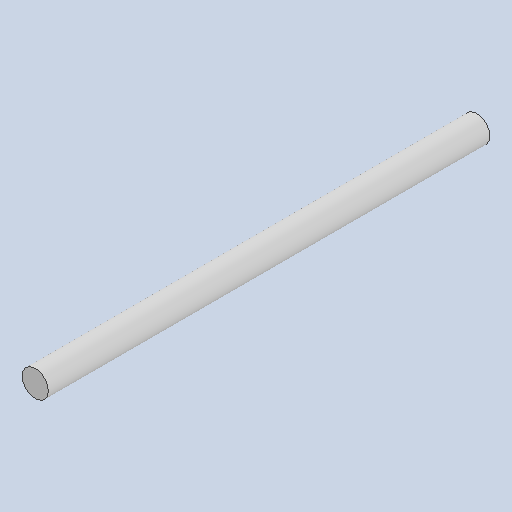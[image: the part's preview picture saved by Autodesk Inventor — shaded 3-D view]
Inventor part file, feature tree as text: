
AUTODESK INVENTOR PART (.ipt)
format: ipt  version: 2023 (Build 270158000, 158)  size: 137,216 bytes
history: native  units: in
note: dims shown in document units (in); Inventor stores cm internally (conversion verified against a paired STEP export)
features: extrude x1, sketch x1
ambient origin geometry x8: Origin, YZ Plane, XZ Plane, XY Plane, X Axis, Y Axis, Z Axis, Center Point
bodies: Solid1 (feature_tree)
feature tree (2):
  extrude  "Extrusion1"  Depth=2.3228in TaperAngle=0.0deg
  sketch  "Sketch1"  dims[d0=0.1378in d1=2.3228in d2=0.0in]
